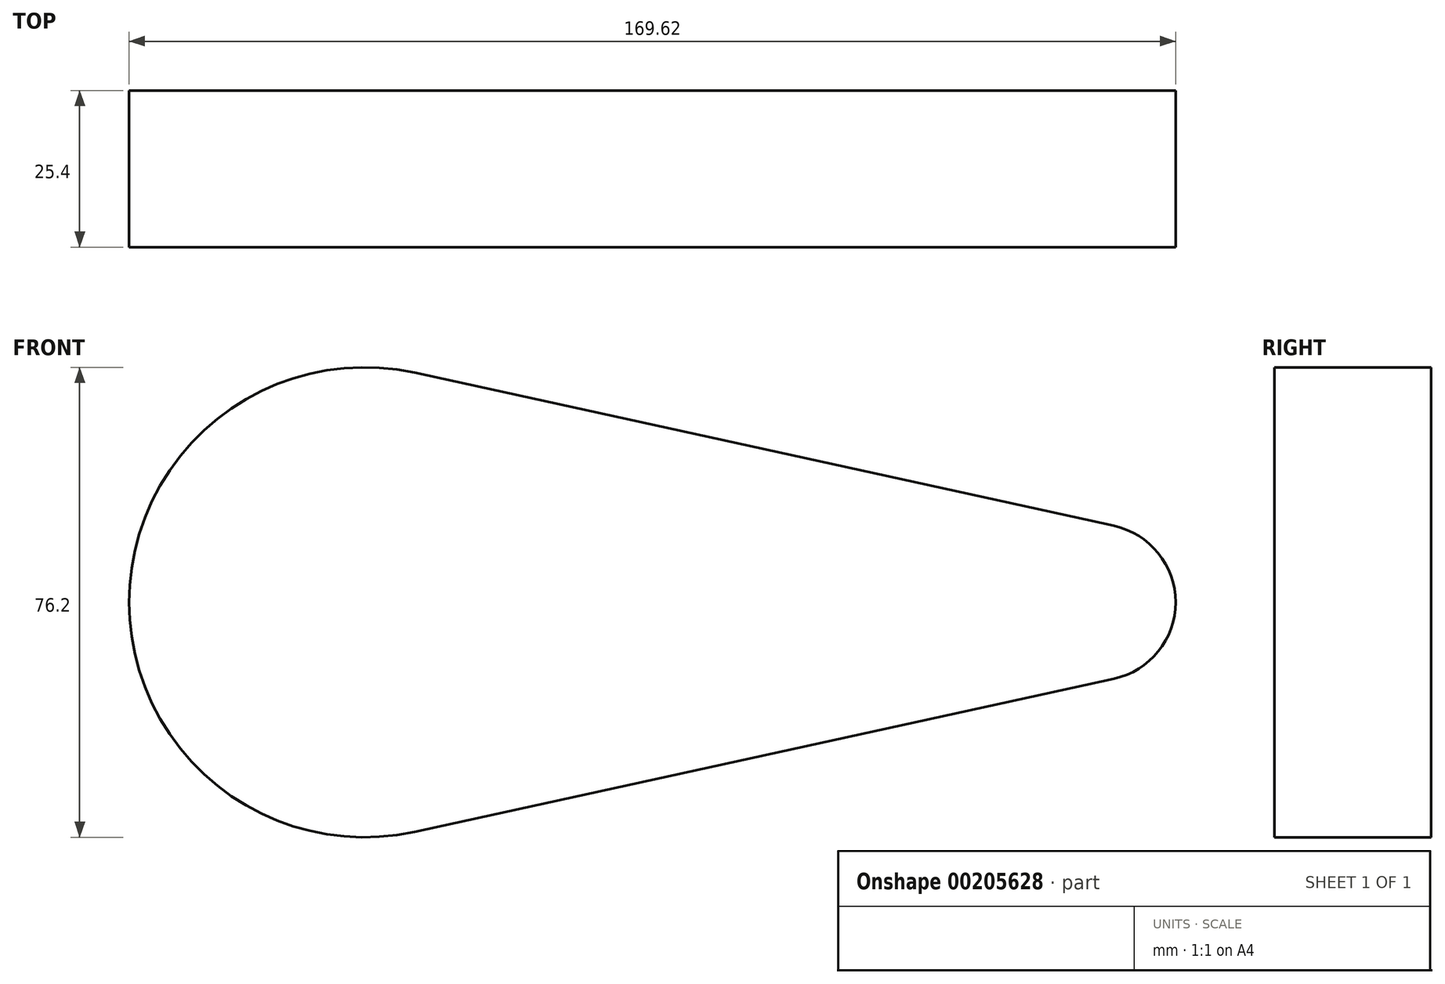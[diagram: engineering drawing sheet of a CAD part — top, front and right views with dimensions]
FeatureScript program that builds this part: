
annotation { "Feature Type Name" : "Feature", "Feature Type Description" : "" }
export const myFeature = defineFeature(function(context is Context, id is Id, definition is map)
    precondition{}
    {
        {
            var Q0;
            Q0=qCreatedBy(makeId("Front.planeOp"),FACE);
            var sketch = newSketch(context, id + "F0", { "sketchPlane" : qUnion([Q0])});
            skCircle(sketch, "E0", {"center": v(0, 0) * mm, "radius": 38.1 * mm});
            skCircle(sketch, "E1", {"center": v(118.82, 0) * mm, "radius": 12.7 * mm});
            skLineSegment(sketch, "E2", {"start": v(8.14, -37.22) * mm, "end": v(121.53, -12.4) * mm});
            skLineSegment(sketch, "E3", {"start": v(8.14, 37.22) * mm, "end": v(121.53, 12.4) * mm});
            skSolve(sketch);
        }
        {
            var Q0;
            {var subQ0=sQuery(id+"F0.wireOp",EDGE,"E0");var subQ1=makeQuery(id+"F0.imprint","INTERSECT",VERTEX,{"derivedFrom":[subQ0,sQuery(id+"F0.wireOp",EDGE,"E2")]});Q0=makeQuery(id+"F0.imprint","IMPRINT",FACE,{"disambiguationData":[TD([[makeQuery(id+"F0.imprint","IMPRINT",EDGE,{"disambiguationData":[TD([[subQ1,1.0]])],"derivedFrom":subQ0}),1.0]])]});}
            var Q1;
            {var subQ0=sQuery(id+"F0.wireOp",EDGE,"E1");var subQ1=makeQuery(id+"F0.imprint","INTERSECT",VERTEX,{"derivedFrom":[subQ0,sQuery(id+"F0.wireOp",EDGE,"E2")]});Q1=makeQuery(id+"F0.imprint","IMPRINT",FACE,{"disambiguationData":[TD([[makeQuery(id+"F0.imprint","IMPRINT",EDGE,{"disambiguationData":[TD([[subQ1,1.0]])],"derivedFrom":subQ0}),1.0]])]});}
            var Q2;
            {var subQ0=sQuery(id+"F0.wireOp",EDGE,"E2");Q2=makeQuery(id+"F0.imprint","IMPRINT",FACE,{"disambiguationData":[TD([[makeQuery(id+"F0.imprint","IMPRINT",EDGE,{"derivedFrom":subQ0}),1.0]])]});}
            extrude(context, id + "F1", {"entities" : qUnion([Q0, Q1, Q2]), "depth" : 25.4 * mm});
        }
        {
            var Q0;
            Q0=makeQuery(id+"F1.opExtrude","CAP_FACE",FACE,{"disambiguationData":[OSD([sQuery(id+"F0.wireOp",EDGE,"E0"),sQuery(id+"F0.wireOp",EDGE,"E1"),sQuery(id+"F0.wireOp",EDGE,"E2"),sQuery(id+"F0.wireOp",EDGE,"E3")])],"isStart":false});
            var sketch = newSketch(context, id + "F2", { "sketchPlane" : qUnion([Q0])});
            skCircle(sketch, "E4", {"center": v(0, 0) * mm, "radius": 12.7 * mm});
            skCircle(sketch, "E5", {"center": v(118.82, 0) * mm, "radius": 7.94 * mm});
            skSolve(sketch);
        }
        {
            var Q0;
            Q0=sQuery(id+"F2.wireOp",EDGE,"E4");
            extrude(context, id + "F3", {"bodyType" : ToolBodyType.SURFACE, "surfaceEntities" : qUnion([Q0]), "oppositeDirection" : true, "depth" : 59.02 * mm});
        }
    });
